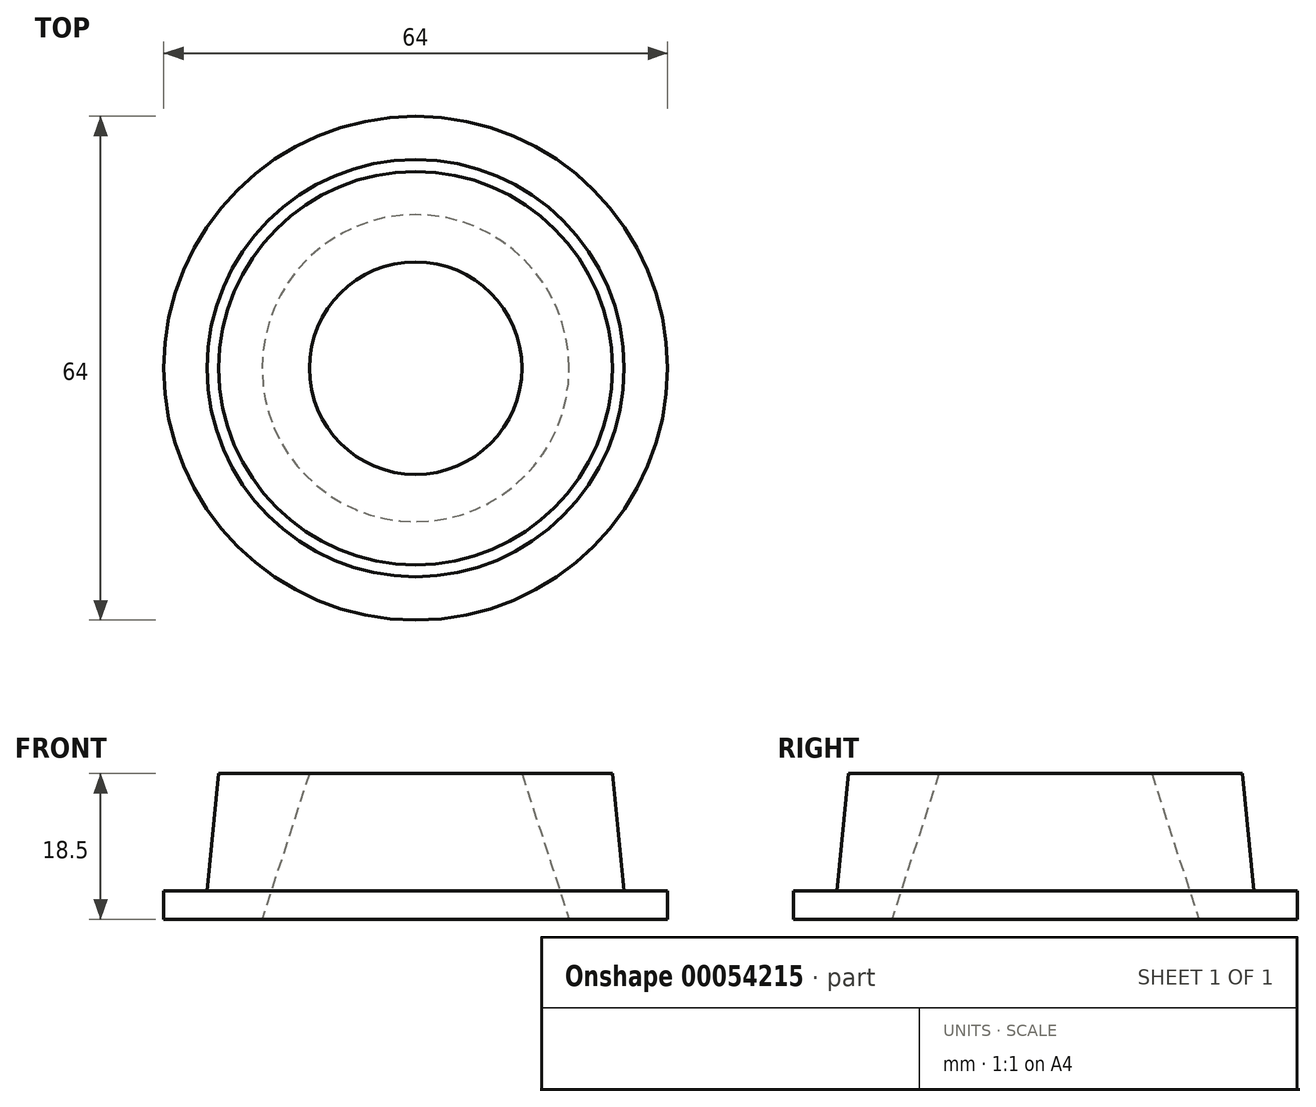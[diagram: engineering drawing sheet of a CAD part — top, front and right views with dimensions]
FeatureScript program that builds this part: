
annotation { "Feature Type Name" : "Feature", "Feature Type Description" : "" }
export const myFeature = defineFeature(function(context is Context, id is Id, definition is map)
    precondition{}
    {
        {
            var Q0;
            Q0=qCreatedBy(makeId("Front.planeOp"),FACE);
            var sketch = newSketch(context, id + "F0", { "sketchPlane" : qUnion([Q0])});
            skLineSegment(sketch, "E0", {"start": v(-32, 3.6) * mm, "end": v(-32, 0) * mm});
            skLineSegment(sketch, "E1", {"start": v(-32, 0) * mm, "end": v(-19.5, 0) * mm});
            skLineSegment(sketch, "E2", {"start": v(-19.5, 0) * mm, "end": v(-13.5, 18.5) * mm});
            skLineSegment(sketch, "E3", {"start": v(-13.5, 18.5) * mm, "end": v(-25, 18.5) * mm});
            skLineSegment(sketch, "E4", {"start": v(-25, 18.5) * mm, "end": v(-26.5, 3.6) * mm});
            skLineSegment(sketch, "E5", {"start": v(-32, 3.6) * mm, "end": v(-26.5, 3.6) * mm});
            skLineSegment(sketch, "E6", {"start": v(-19.5, 0) * mm, "end": v(0, 0) * mm});
            skLineSegment(sketch, "E7", {"start": v(0, 0) * mm, "end": v(0, -6.77) * mm});
            skSolve(sketch);
        }
        {
            var Q0;
            Q0=makeQuery(id+"F0.imprint","IMPRINT",FACE,{"disambiguationData":[TD([[makeQuery(id+"F0.imprint","IMPRINT",EDGE,{"derivedFrom":sQuery(id+"F0.wireOp",EDGE,"E0")}),1.0]])]});
            var Q1;
            Q1=sQuery(id+"F0.wireOp",EDGE,"E7");
            revolve(context, id + "F1", {"entities" : qUnion([Q0]), "axis" : qUnion([Q1]), "revolveType" : RevolveType.FULL});
        }
    });
